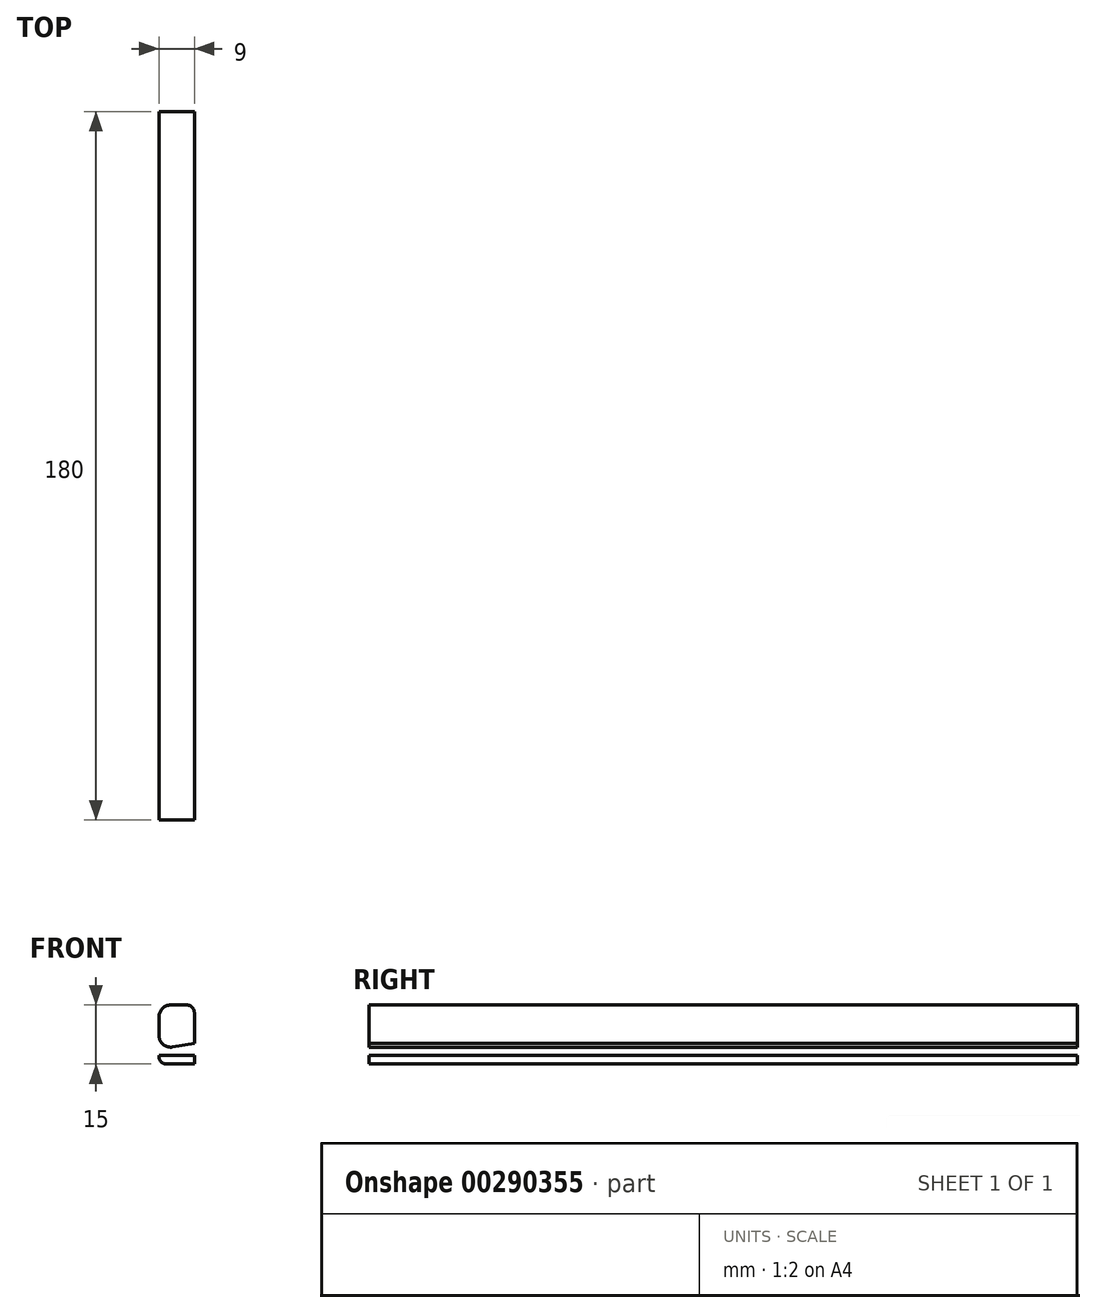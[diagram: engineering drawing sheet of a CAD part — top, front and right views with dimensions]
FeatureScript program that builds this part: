
annotation { "Feature Type Name" : "Feature", "Feature Type Description" : "" }
export const myFeature = defineFeature(function(context is Context, id is Id, definition is map)
    precondition{}
    {
        {
            var Q0;
            Q0=qCreatedBy(makeId("Front.planeOp"),FACE);
            var sketch = newSketch(context, id + "F0", { "sketchPlane" : qUnion([Q0])});
            skLineSegment(sketch, "E0.bottom", {"start": v(7.5, 7.5) * mm, "end": v(-7.5, 7.5) * mm});
            skLineSegment(sketch, "E0.top", {"start": v(7.5, -7.5) * mm, "end": v(-7.5, -7.5) * mm});
            skLineSegment(sketch, "E0.left", {"start": v(7.5, 7.5) * mm, "end": v(7.5, -7.5) * mm});
            skLineSegment(sketch, "E0.right", {"start": v(-7.5, 7.5) * mm, "end": v(-7.5, -7.5) * mm});
            skPoint(sketch, "E0.middle", {"position": v(0, 0) * mm});
            skLineSegment(sketch, "E1.bottom", {"start": v(-7.5, 7.5) * mm, "end": v(1.5, 7.5) * mm});
            skLineSegment(sketch, "E1.right", {"start": v(1.5, 7.5) * mm, "end": v(1.5, 0) * mm});
            skLineSegment(sketch, "E2", {"start": v(1.5, 0) * mm, "end": v(-7.5, -1.5) * mm});
            skLineSegment(sketch, "E3.0", {"start": v(1.5, -2.25) * mm, "end": v(-7.5, -3.75) * mm});
            skLineSegment(sketch, "E4", {"start": v(1.5, 0) * mm, "end": v(1.5, -2.25) * mm});
            skPoint(sketch, "E5", {"position": v(-7.5, -5.25) * mm});
            skLineSegment(sketch, "E6", {"start": v(1.5, -2.25) * mm, "end": v(1.5, -7.5) * mm});
            skLineSegment(sketch, "E7", {"start": v(-7.5, -5.25) * mm, "end": v(1.5, -5.25) * mm});
            skSolve(sketch);
        }
        {
            var Q0;
            {var subQ0=sQuery(id+"F0.wireOp",EDGE,"E2");Q0=makeQuery(id+"F0.imprint","IMPRINT",FACE,{"disambiguationData":[TD([[makeQuery(id+"F0.imprint","IMPRINT",EDGE,{"derivedFrom":subQ0}),1.0]])]});}
            var Q1;
            Q1=makeQuery(id+"F0.imprint","IMPRINT",FACE,{"disambiguationData":[TD([[makeQuery(id+"F0.imprint","IMPRINT",EDGE,{"derivedFrom":sQuery(id+"F0.wireOp",EDGE,"E0.bottom")}),1.0]])]});
            var Q2;
            {var subQ5=sQuery(id+"F0.wireOp",EDGE,"E7");Q2=makeQuery(id+"F0.imprint","IMPRINT",FACE,{"disambiguationData":[TD([[makeQuery(id+"F0.imprint","IMPRINT",EDGE,{"derivedFrom":subQ5}),-1.0]])]});}
            extrude(context, id + "F1", {"entities" : qUnion([Q0, Q1, Q2]), "oppositeDirection" : true, "depth" : 180 * mm});
        }
        {
            var Q0;
            Q0=makeQuery(id+"F1.opExtrude","SWEPT_EDGE",EDGE,{"disambiguationData":[OSD([sQuery(id+"F0.wireOp",EDGE,"E0.right"),sQuery(id+"F0.wireOp",EDGE,"E2")])]});
            fillet(context, id + "F2", {"entities" : qUnion([Q0]), "radius" : 3 * mm, "tangentPropagation" : true, "allowEdgeOverflow" : false});
        }
        {
            var Q0;
            Q0=makeQuery(id+"F1.opExtrude","SWEPT_EDGE",EDGE,{"disambiguationData":[OSD([sQuery(id+"F0.wireOp",EDGE,"E0.top"),sQuery(id+"F0.wireOp",EDGE,"E0.right")])]});
            fillet(context, id + "F3", {"entities" : qUnion([Q0]), "radius" : 2 * mm, "tangentPropagation" : true, "allowEdgeOverflow" : false});
        }
        {
            var Q0;
            Q0=makeQuery(id+"F1.opExtrude","SWEPT_EDGE",EDGE,{"disambiguationData":[OSD([sQuery(id+"F0.wireOp",EDGE,"E0.bottom"),sQuery(id+"F0.wireOp",EDGE,"E1.bottom"),sQuery(id+"F0.wireOp",EDGE,"E1.right")])]});
            var Q1;
            Q1=makeQuery(id+"F1.opExtrude","SWEPT_EDGE",EDGE,{"disambiguationData":[OSD([sQuery(id+"F0.wireOp",EDGE,"E0.bottom"),sQuery(id+"F0.wireOp",EDGE,"E0.left")])]});
            fillet(context, id + "F4", {"entities" : qUnion([Q0, Q1]), "radius" : 1.9 * mm, "tangentPropagation" : true, "allowEdgeOverflow" : false});
        }
    });
